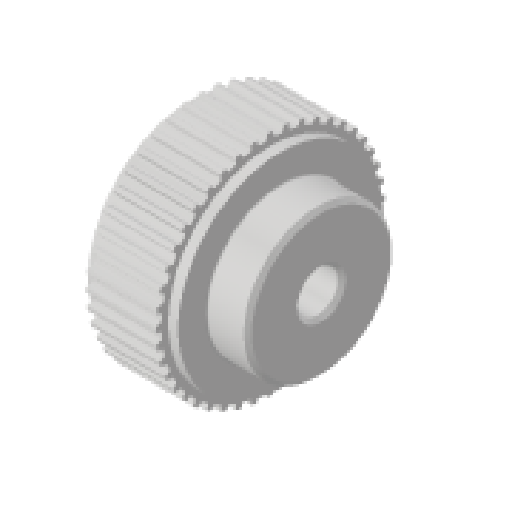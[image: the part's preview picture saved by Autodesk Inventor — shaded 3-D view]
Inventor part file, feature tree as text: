
AUTODESK INVENTOR PART (.ipt)
format: ipt  version: 2025.1 (Build 291241000, 241)  size: 625,664 bytes
history: native  units: mm
features: other x21, sketch x2, revolve x1, extrude x1
ambient origin geometry x8: Origin, YZ Plane, XZ Plane, XY Plane, X Axis, Y Axis, Z Axis, Center Point
bodies: Solid1 (feature_tree)
feature tree (25):
  revolve  "Revolution1"  [1 undecoded]
  extrude  "Extrusion1"  TaperAngle=0.0deg  [1 undecoded]
  other  "FLL_XY"
  other  "FLL_YZ"
  other  "FLL_ZX"
  other  "FLL_X"
  other  "FLL_Y"
  other  "FLL_Z"
  other  "FLL_Center"
  other  "FLR_XY"
  other  "FLR_YZ"
  other  "FLR_ZX"
  other  "FLR_X"
  other  "FLR_Y"
  other  "FLR_Z"
  other  "FLR_Center"
  other  "MXL025_D_XY"
  other  "MXL025_D_YZ"
  other  "MXL025_D_ZX"
  other  "MXL025_D_X"
  other  "MXL025_D_Y"
  other  "MXL025_D_Z"
  other  "MXL025_D_Center"
  sketch  "Sketch_5"  dims[d3=0.0mm d4=0.0mm d5=0.0mm]
  sketch  "Sketch_3"  dims[d0=360.0deg d1=11.0mm d2=0.0mm]
note: 2 required parameter values undecoded (feature->parameter linkage not recoverable at this tier; creation-order binding heuristic only, values carry confidence <= 0.55)